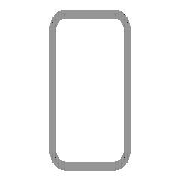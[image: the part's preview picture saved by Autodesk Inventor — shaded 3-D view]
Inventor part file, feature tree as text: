
AUTODESK INVENTOR PART (.ipt)
format: ipt  version: 2025 (Build 290162010, 162A)  size: 153,600 bytes
history: native  units: mm (DEFAULTED — no unit token found)
features: other x3, sketch x2, projected_geometry x2, extrude x1, plane x1
ambient origin geometry x8: Origin, YZ Plane, XZ Plane, XY Plane, X Axis, Y Axis, Z Axis, Center Point
bodies: Solid1 (feature_tree), Body (feature_tree)
feature tree (9):
  other  "Driven Length"
  other  "Start plane"
  other  "End plane"
  extrude  "Extrusion2"  TaperAngle=0.0deg  [1 undecoded]
  sketch  "Sketch3"  dims[d3=2000.0mm d4=0.0mm]
  plane  "Work Plane3"
  sketch  "Sketch5"  dims[d7=4.0mm d9=20.0mm d11=40.0mm d12=2.0mm d13=-0.0mm d14=2000.0mm d15=10.0mm d16=20.0mm d17=90.0deg d18=2000.0mm d19=9.599311mm d20=6.108652mm d21=0.0mm d22=0.0mm]
  projected_geometry  "Projected Loop1"
  projected_geometry  "Projected Loop2"
note: 1 required parameter value undecoded (feature->parameter linkage not recoverable at this tier; creation-order binding heuristic only, values carry confidence <= 0.55)
